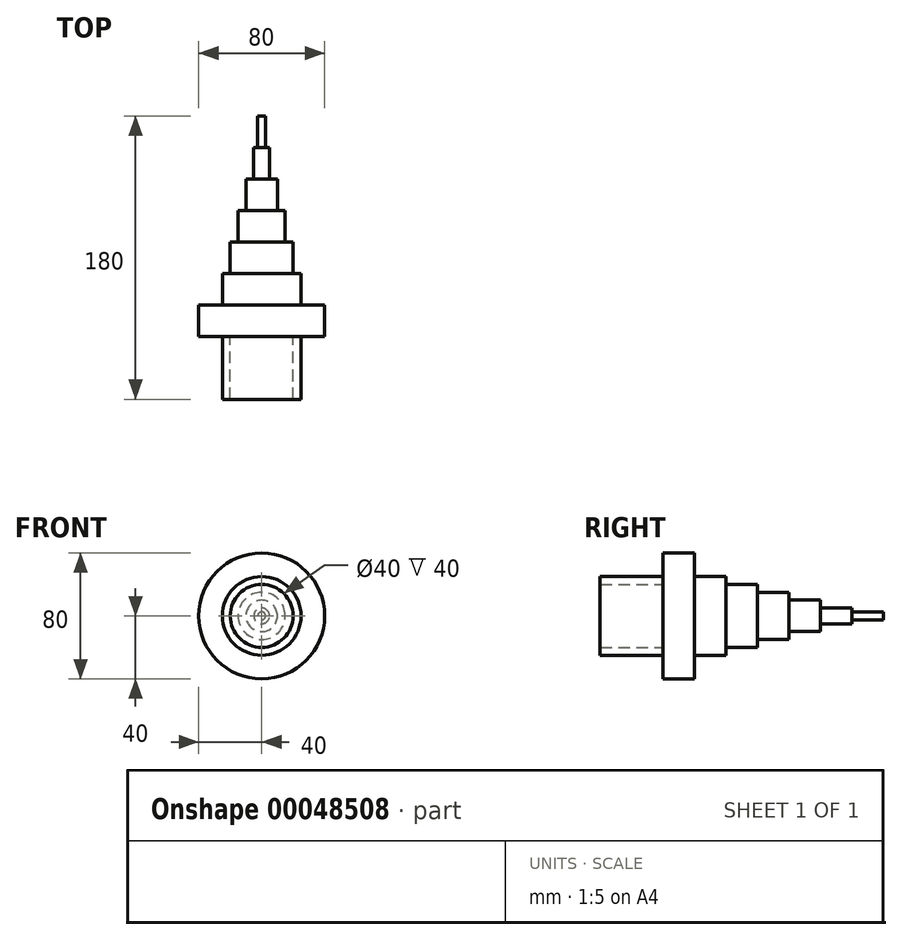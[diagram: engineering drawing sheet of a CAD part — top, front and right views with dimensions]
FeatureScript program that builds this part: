
annotation { "Feature Type Name" : "Feature", "Feature Type Description" : "" }
export const myFeature = defineFeature(function(context is Context, id is Id, definition is map)
    precondition{}
    {
        {
            var Q0;
            Q0=qCreatedBy(makeId("Right.planeOp"),FACE);
            var sketch = newSketch(context, id + "F0", { "sketchPlane" : qUnion([Q0])});
            skLineSegment(sketch, "E0", {"start": v(0, 0) * mm, "end": v(0, 25) * mm});
            skLineSegment(sketch, "E1", {"start": v(0, 25) * mm, "end": v(40, 25) * mm});
            skLineSegment(sketch, "E2", {"start": v(40, 25) * mm, "end": v(40, 40) * mm});
            skLineSegment(sketch, "E3", {"start": v(40, 40) * mm, "end": v(60, 40) * mm});
            skLineSegment(sketch, "E4", {"start": v(60, 40) * mm, "end": v(60, 25) * mm});
            skLineSegment(sketch, "E5", {"start": v(60, 25) * mm, "end": v(80, 25) * mm});
            skLineSegment(sketch, "E6", {"start": v(80, 25) * mm, "end": v(80, 20) * mm});
            skLineSegment(sketch, "E7", {"start": v(80, 20) * mm, "end": v(100, 20) * mm});
            skLineSegment(sketch, "E8", {"start": v(100, 20) * mm, "end": v(100, 15) * mm});
            skLineSegment(sketch, "E9", {"start": v(100, 15) * mm, "end": v(120, 15) * mm});
            skLineSegment(sketch, "E10", {"start": v(120, 15) * mm, "end": v(120, 10) * mm});
            skLineSegment(sketch, "E11", {"start": v(120, 10) * mm, "end": v(140, 10) * mm});
            skLineSegment(sketch, "E12", {"start": v(140, 10) * mm, "end": v(140, 5) * mm});
            skLineSegment(sketch, "E13", {"start": v(140, 5) * mm, "end": v(160, 5) * mm});
            skLineSegment(sketch, "E14", {"start": v(160, 5) * mm, "end": v(160, 2.5) * mm});
            skLineSegment(sketch, "E15", {"start": v(160, 2.5) * mm, "end": v(180, 2.5) * mm});
            skLineSegment(sketch, "E16", {"start": v(180, 2.5) * mm, "end": v(180, 0) * mm});
            skLineSegment(sketch, "E17", {"start": v(180, 0) * mm, "end": v(0, 0) * mm});
            skLineSegment(sketch, "E18", {"start": v(0, 20) * mm, "end": v(40, 20) * mm});
            skLineSegment(sketch, "E19", {"start": v(40, 20) * mm, "end": v(40, 0) * mm});
            skSolve(sketch);
        }
        {
            var Q0;
            {var subQ4=sQuery(id+"F0.wireOp",EDGE,"E1");Q0=makeQuery(id+"F0.imprint","IMPRINT",FACE,{"disambiguationData":[TD([[makeQuery(id+"F0.imprint","IMPRINT",EDGE,{"derivedFrom":subQ4}),-1.0]])]});}
            var Q1;
            Q1=sQuery(id+"F0.wireOp",EDGE,"E17");
            revolve(context, id + "F1", {"entities" : qUnion([Q0]), "axis" : qUnion([Q1]), "revolveType" : RevolveType.FULL});
        }
    });
